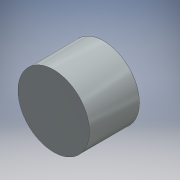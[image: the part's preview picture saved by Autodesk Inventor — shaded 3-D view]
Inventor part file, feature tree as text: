
AUTODESK INVENTOR PART (.ipt)
format: ipt  version: 2016 (Build 200138000, 138)  size: 138,240 bytes
history: native  units: mm
features: extrude x4, sketch x4
ambient origin geometry x8: Origin, YZ Plane, XZ Plane, XY Plane, X Axis, Y Axis, Z Axis, Center Point
bodies: Solid1 (feature_tree)
feature tree (8):
  extrude  "Extrusion1"  Depth=21.0mm TaperAngle=0.0deg
  extrude  "Extrusion2"  Depth=1.5mm
  extrude  "Extrusion3"  Depth=1.0mm
  extrude  "Extrusion4"  Depth=6.0mm
  sketch  "Sketch1"  dims[d0=30.0mm d1=21.0mm d2=0.0mm]
  sketch  "Sketch2"  dims[d3=4.5mm d4=1.5mm]
  sketch  "Sketch3"  dims[d5=1.0mm d6=0.0mm d7=3.0mm]
  sketch  "Sketch4"  dims[d8=2.5mm d9=0.0mm d10=3.0mm d11=0.5mm d12=0.5mm d13=6.0mm d14=0.0mm]
